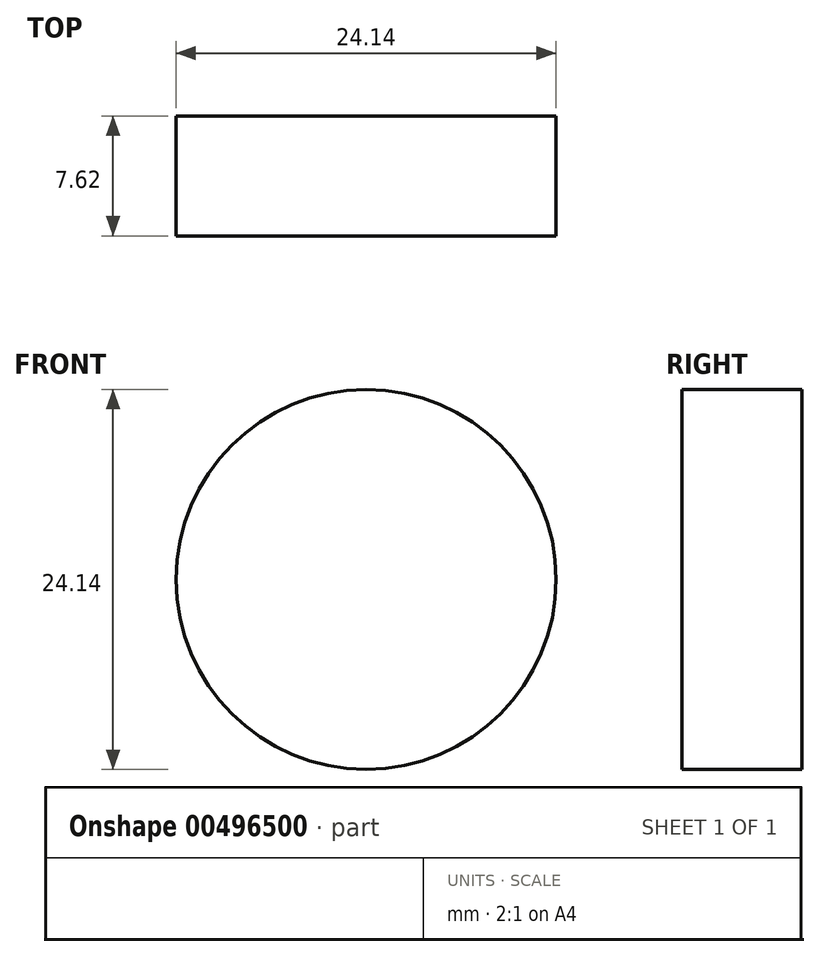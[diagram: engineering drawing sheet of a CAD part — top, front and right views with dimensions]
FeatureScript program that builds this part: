
annotation { "Feature Type Name" : "Feature", "Feature Type Description" : "" }
export const myFeature = defineFeature(function(context is Context, id is Id, definition is map)
    precondition{}
    {
        {
            var Q0;
            Q0=qCreatedBy(makeId("Front.planeOp"),FACE);
            var sketch = newSketch(context, id + "F0", { "sketchPlane" : qUnion([Q0])});
            skCircle(sketch, "E0", {"center": v(0, 0) * mm, "radius": 12.07 * mm});
            skSolve(sketch);
        }
        {
            var Q0;
            Q0 = qSketchRegion(id + "F0", true);
            extrude(context, id + "F1", {"entities" : qUnion([Q0]), "endBound" : BoundingType.SYMMETRIC, "depth" : 7.62 * mm});
        }
    });
